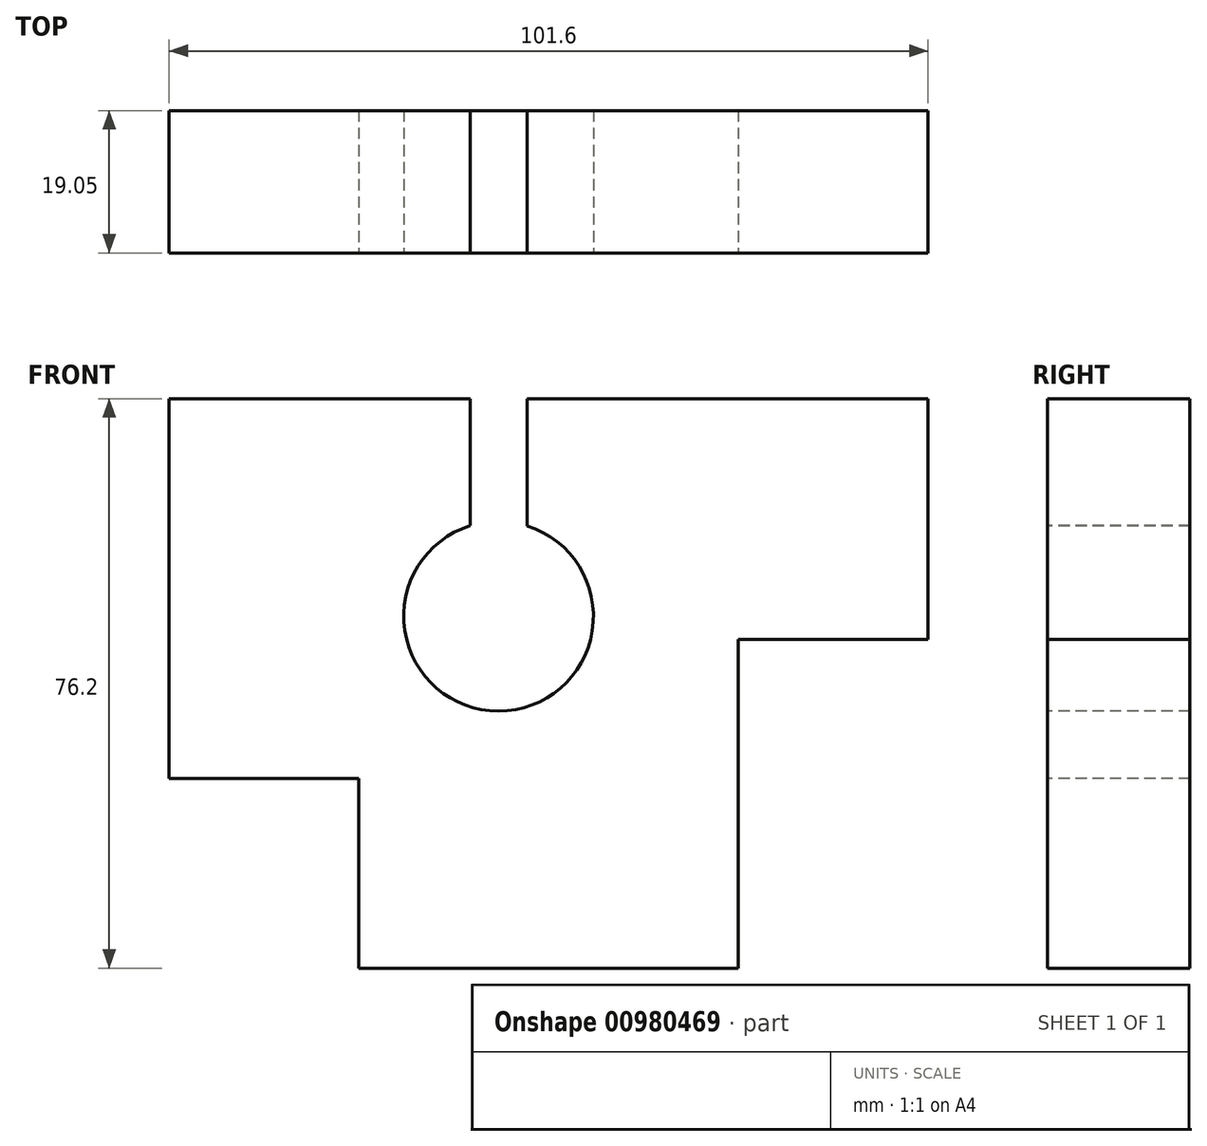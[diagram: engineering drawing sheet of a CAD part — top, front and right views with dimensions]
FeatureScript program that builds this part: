
annotation { "Feature Type Name" : "Feature", "Feature Type Description" : "" }
export const myFeature = defineFeature(function(context is Context, id is Id, definition is map)
    precondition{}
    {
        {
            var Q0;
            Q0=qCreatedBy(makeId("Front.planeOp"),FACE);
            var sketch = newSketch(context, id + "F0", { "sketchPlane" : qUnion([Q0])});
            skLineSegment(sketch, "E0.bottom", {"start": v(-113.48, 38) * mm, "end": v(-11.88, 38) * mm});
            skLineSegment(sketch, "E0.top", {"start": v(-113.48, -38.2) * mm, "end": v(-11.88, -38.2) * mm});
            skLineSegment(sketch, "E0.left", {"start": v(-113.48, 38) * mm, "end": v(-113.48, -38.2) * mm});
            skLineSegment(sketch, "E0.right", {"start": v(-11.88, 38) * mm, "end": v(-11.88, -38.2) * mm});
            skSolve(sketch);
        }
        {
            var Q0;
            Q0=makeQuery(id+"F0.imprint","IMPRINT",FACE,{"disambiguationData":[TD([[makeQuery(id+"F0.imprint","IMPRINT",EDGE,{"derivedFrom":sQuery(id+"F0.wireOp",EDGE,"E0.bottom")}),-1.0]])]});
            extrude(context, id + "F1", {"entities" : qUnion([Q0]), "depth" : 19.05 * mm, "offsetDistance" : 25.4 * mm});
        }
        {
            var Q0;
            Q0=makeQuery(id+"F1.opExtrude","CAP_FACE",FACE,{"disambiguationData":[OSD([sQuery(id+"F0.wireOp",EDGE,"E0.bottom"),sQuery(id+"F0.wireOp",EDGE,"E0.top"),sQuery(id+"F0.wireOp",EDGE,"E0.left"),sQuery(id+"F0.wireOp",EDGE,"E0.right")])],"isStart":false});
            var sketch = newSketch(context, id + "F2", { "sketchPlane" : qUnion([Q0])});
            skLineSegment(sketch, "E1.bottom", {"start": v(-113.48, -38.2) * mm, "end": v(-88.08, -38.2) * mm});
            skLineSegment(sketch, "E1.top", {"start": v(-113.48, -12.8) * mm, "end": v(-88.08, -12.8) * mm});
            skLineSegment(sketch, "E1.left", {"start": v(-113.48, -38.2) * mm, "end": v(-113.48, -12.8) * mm});
            skLineSegment(sketch, "E1.right", {"start": v(-88.08, -38.2) * mm, "end": v(-88.08, -12.8) * mm});
            skSolve(sketch);
        }
        {
            var Q0;
            Q0=makeQuery(id+"F2.imprint","IMPRINT",FACE,{"disambiguationData":[TD([[makeQuery(id+"F2.imprint","IMPRINT",EDGE,{"derivedFrom":sQuery(id+"F2.wireOp",EDGE,"E1.bottom")}),1.0]])]});
            extrude(context, id + "F3", {"entities" : qUnion([Q0]), "operationType" : NewBodyOperationType.REMOVE, "oppositeDirection" : true, "depth" : 19.05 * mm, "offsetDistance" : 25.4 * mm});
        }
        {
            var Q0;
            Q0=makeQuery(id+"F1.opExtrude","CAP_FACE",FACE,{"disambiguationData":[OSD([sQuery(id+"F0.wireOp",EDGE,"E0.bottom"),sQuery(id+"F0.wireOp",EDGE,"E0.top"),sQuery(id+"F0.wireOp",EDGE,"E0.left"),sQuery(id+"F0.wireOp",EDGE,"E0.right")])],"isStart":false});
            var sketch = newSketch(context, id + "F4", { "sketchPlane" : qUnion([Q0])});
            skLineSegment(sketch, "E2.bottom", {"start": v(-11.88, -38.2) * mm, "end": v(-37.28, -38.2) * mm});
            skLineSegment(sketch, "E2.top", {"start": v(-11.88, 5.8) * mm, "end": v(-37.28, 5.8) * mm});
            skLineSegment(sketch, "E2.left", {"start": v(-11.88, -38.2) * mm, "end": v(-11.88, 5.8) * mm});
            skLineSegment(sketch, "E2.right", {"start": v(-37.28, -38.2) * mm, "end": v(-37.28, 5.8) * mm});
            skSolve(sketch);
        }
        {
            var Q0;
            Q0=makeQuery(id+"F4.imprint","IMPRINT",FACE,{"disambiguationData":[TD([[makeQuery(id+"F4.imprint","IMPRINT",EDGE,{"derivedFrom":sQuery(id+"F4.wireOp",EDGE,"E2.bottom")}),1.0]])]});
            extrude(context, id + "F5", {"entities" : qUnion([Q0]), "operationType" : NewBodyOperationType.REMOVE, "oppositeDirection" : true, "depth" : 19.05 * mm, "offsetDistance" : 25.4 * mm});
        }
        {
            var Q0;
            Q0=makeQuery(id+"F1.opExtrude","CAP_FACE",FACE,{"disambiguationData":[OSD([sQuery(id+"F0.wireOp",EDGE,"E0.bottom"),sQuery(id+"F0.wireOp",EDGE,"E0.top"),sQuery(id+"F0.wireOp",EDGE,"E0.left"),sQuery(id+"F0.wireOp",EDGE,"E0.right")])],"isStart":false});
            var sketch = newSketch(context, id + "F6", { "sketchPlane" : qUnion([Q0])});
            skCircle(sketch, "E3", {"center": v(-69.38, 8.89) * mm, "radius": 12.7 * mm});
            skSolve(sketch);
        }
        {
            var Q0;
            Q0=makeQuery(id+"F6.imprint","IMPRINT",FACE,{"disambiguationData":[TD([[makeQuery(id+"F6.imprint","IMPRINT",EDGE,{"derivedFrom":sQuery(id+"F6.wireOp",EDGE,"E3")}),1.0]])]});
            extrude(context, id + "F7", {"entities" : qUnion([Q0]), "operationType" : NewBodyOperationType.REMOVE, "oppositeDirection" : true, "depth" : 19.05 * mm, "offsetDistance" : 25.4 * mm});
        }
        {
            var Q0;
            Q0=makeQuery(id+"F1.opExtrude","CAP_FACE",FACE,{"disambiguationData":[OSD([sQuery(id+"F0.wireOp",EDGE,"E0.bottom"),sQuery(id+"F0.wireOp",EDGE,"E0.top"),sQuery(id+"F0.wireOp",EDGE,"E0.left"),sQuery(id+"F0.wireOp",EDGE,"E0.right")])],"isStart":false});
            var sketch = newSketch(context, id + "F8", { "sketchPlane" : qUnion([Q0])});
            skLineSegment(sketch, "E4.bottom", {"start": v(-73.18, 38) * mm, "end": v(-65.56, 38) * mm});
            skLineSegment(sketch, "E4.top", {"start": v(-73.18, 12.6) * mm, "end": v(-65.56, 12.6) * mm});
            skLineSegment(sketch, "E4.left", {"start": v(-73.18, 38) * mm, "end": v(-73.18, 12.6) * mm});
            skLineSegment(sketch, "E4.right", {"start": v(-65.56, 38) * mm, "end": v(-65.56, 12.6) * mm});
            skSolve(sketch);
        }
        {
            var Q0;
            {var subQ0=sQuery(id+"F8.wireOp",EDGE,"E4.bottom");Q0=makeQuery(id+"F8.imprint","IMPRINT",FACE,{"disambiguationData":[TD([[makeQuery(id+"F8.imprint","IMPRINT",EDGE,{"derivedFrom":subQ0}),-1.0]])]});}
            extrude(context, id + "F9", {"entities" : qUnion([Q0]), "operationType" : NewBodyOperationType.REMOVE, "endBound" : BoundingType.UP_TO_NEXT, "oppositeDirection" : true, "depth" : 25.4 * mm, "offsetDistance" : 25.4 * mm});
        }
    });
